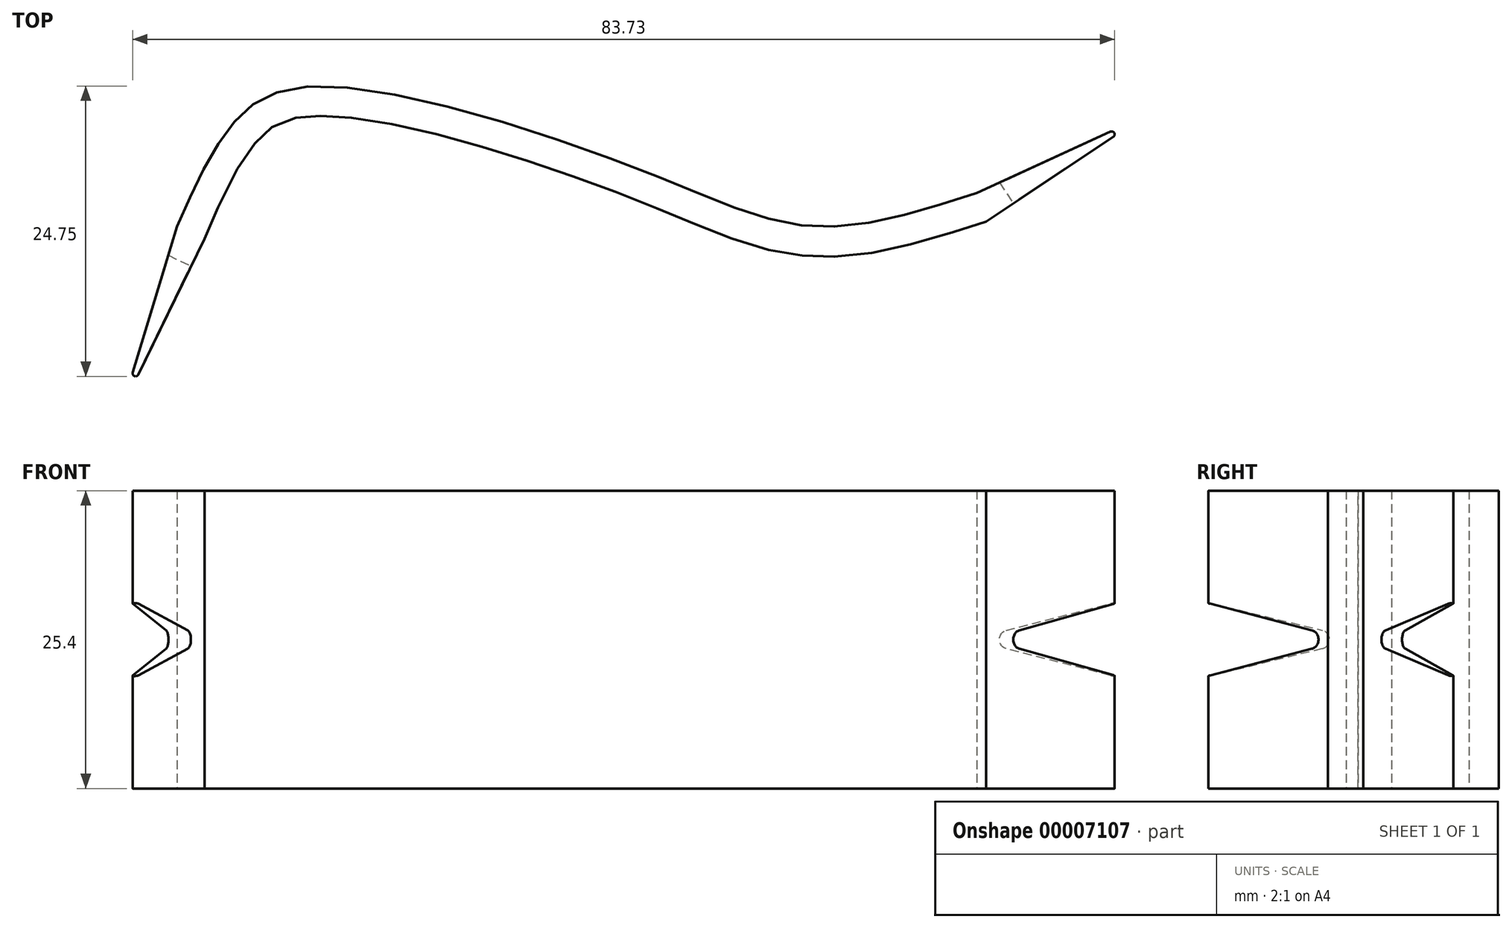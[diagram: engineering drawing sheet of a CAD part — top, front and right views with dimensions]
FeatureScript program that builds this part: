
annotation { "Feature Type Name" : "Feature", "Feature Type Description" : "" }
export const myFeature = defineFeature(function(context is Context, id is Id, definition is map)
    precondition{}
    {
        {
            var Q0;
            Q0=qCreatedBy(makeId("Top.planeOp"),FACE);
            var sketch = newSketch(context, id + "F0", { "sketchPlane" : qUnion([Q0])});
            skFitSpline(sketch, "E0", {"points": [v(0, 0) * mm, v(4.54, 8.52) * mm, v(11.67, 11.97) * mm, v(39.9, 4.7) * mm, v(54.55, 0) * mm, v(68.2, 2.86) * mm], "startDerivative": vector(25.3, 57.5) * mm, "endDerivative": vector(71.65, 23.12) * mm});
            skFitSpline(sketch, "E1.0", {"points": [v(2.33, -1.02) * mm, v(2.85, 0.18) * mm, v(3.89, 2.52) * mm, v(5.22, 5.08) * mm, v(6.2, 6.52) * mm, v(6.75, 7.22) * mm, v(7.3, 7.82) * mm, v(7.98, 8.4) * mm, v(8.9, 8.92) * mm, v(9.87, 9.23) * mm, v(10.88, 9.38) * mm, v(11.76, 9.44) * mm, v(12.78, 9.44) * mm, v(14.32, 9.35) * mm, v(16.52, 9.07) * mm, v(19.5, 8.5) * mm, v(22.68, 7.73) * mm, v(26, 6.81) * mm, v(29.34, 5.78) * mm, v(32.65, 4.68) * mm, v(35.82, 3.54) * mm, v(38.77, 2.42) * mm, v(41.42, 1.35) * mm, v(43.86, 0.34) * mm, v(46.14, -0.58) * mm, v(48.35, -1.38) * mm, v(50.55, -2.01) * mm, v(52.42, -2.37) * mm, v(53.96, -2.52) * mm, v(55.53, -2.58) * mm, v(57.48, -2.47) * mm, v(59.82, -2.13) * mm, v(62.13, -1.61) * mm, v(65.2, -0.78) * mm, v(67.48, -0.04) * mm, v(68.97, 0.44) * mm]});
            skLineSegment(sketch, "E2", {"start": v(68.2, 2.86) * mm, "end": v(82.55, 9.46) * mm});
            skLineSegment(sketch, "E3", {"start": v(82.55, 9.46) * mm, "end": v(68.97, 0.44) * mm});
            skLineSegment(sketch, "E4", {"start": v(0, 0) * mm, "end": v(-4.72, -15.53) * mm});
            skLineSegment(sketch, "E5", {"start": v(-4.72, -15.53) * mm, "end": v(2.33, -1.02) * mm});
            skSolve(sketch);
        }
        {
            var Q0;
            Q0 = qSketchRegion(id + "F0", true);
            extrude(context, id + "F1", {"entities" : qUnion([Q0]), "depth" : 25.4 * mm});
        }
        {
            var Q0;
            Q0=makeQuery(id+"F1.opExtrude","SWEPT_FACE",FACE,{"disambiguationData":[OSD([sQuery(id+"F0.wireOp",EDGE,"E5")])]});
            var sketch = newSketch(context, id + "F2", { "sketchPlane" : qUnion([Q0])});
            skLineSegment(sketch, "E6", {"start": v(-16.03, 16.51) * mm, "end": v(-3.15, 13.49) * mm});
            skLineSegment(sketch, "E7", {"start": v(-3.15, 11.91) * mm, "end": v(-16.03, 8.89) * mm});
            skLineSegment(sketch, "E8", {"start": v(-16.03, 8.9) * mm, "end": v(-16.03, 16.51) * mm});
            skLineSegment(sketch, "E9", {"start": v(-16.03, 16.51) * mm, "end": v(-16.03, 25.4) * mm, "construction": true});
            skLineSegment(sketch, "E10", {"start": v(-16.03, 25.4) * mm, "end": v(-16.03, 16.51) * mm, "construction": true});
            skLineSegment(sketch, "E11", {"start": v(-16.03, 8.9) * mm, "end": v(-16.03, 0) * mm, "construction": true});
            skPoint(sketch, "E12.visualSharp", {"position": v(0.2, 12.7) * mm});
            skArc(sketch, "E12.filletArc", {"start": v(-3.15, 11.91) * mm, "mid": v(-2.53, 12.7) * mm, "end": v(-3.15, 13.49) * mm});
            skLineSegment(sketch, "E13", {"start": v(-16.03, 12.7) * mm, "end": v(-3.33, 12.7) * mm, "construction": true});
            skSolve(sketch);
        }
        {
            var Q0;
            Q0 = qSketchRegion(id + "F2", true);
            extrude(context, id + "F3", {"entities" : qUnion([Q0]), "operationType" : NewBodyOperationType.REMOVE, "oppositeDirection" : true, "depth" : 25.4 * mm});
        }
        {
            var Q0;
            Q0=makeQuery(id+"F1.opExtrude","SWEPT_FACE",FACE,{"disambiguationData":[OSD([sQuery(id+"F0.wireOp",EDGE,"E3")])]});
            var sketch = newSketch(context, id + "F4", { "sketchPlane" : qUnion([Q0])});
            skLineSegment(sketch, "E14", {"start": v(73.99, 16.51) * mm, "end": v(61.1, 13.49) * mm});
            skLineSegment(sketch, "E15", {"start": v(61.1, 11.91) * mm, "end": v(73.99, 8.89) * mm});
            skLineSegment(sketch, "E16", {"start": v(73.99, 8.9) * mm, "end": v(73.99, 16.51) * mm});
            skPoint(sketch, "E17.visualSharp", {"position": v(57.75, 12.7) * mm});
            skArc(sketch, "E17.filletArc", {"start": v(61.1, 13.49) * mm, "mid": v(60.48, 12.7) * mm, "end": v(61.1, 11.91) * mm});
            skLineSegment(sketch, "E18", {"start": v(73.99, 16.51) * mm, "end": v(73.99, 25.4) * mm, "construction": true});
            skLineSegment(sketch, "E19", {"start": v(73.99, 8.9) * mm, "end": v(73.99, 0) * mm, "construction": true});
            skLineSegment(sketch, "E20", {"start": v(61.29, 12.7) * mm, "end": v(73.99, 12.7) * mm, "construction": true});
            skSolve(sketch);
        }
        {
            var Q0;
            Q0 = qSketchRegion(id + "F4", true);
            extrude(context, id + "F5", {"entities" : qUnion([Q0]), "operationType" : NewBodyOperationType.REMOVE, "oppositeDirection" : true, "depth" : 25.4 * mm});
        }
        {
            var Q0;
            {var subQ0=sQuery(id+"F0.wireOp",EDGE,"E4");var subQ1=sQuery(id+"F0.wireOp",EDGE,"E5");Q0=makeQuery(id+"F3.boolean.opBoolean","SPLIT",EDGE,{"disambiguationData":[TD([makeQuery(id+"F3.opExtrude","SWEPT_FACE",FACE,{"disambiguationData":[OSD([sQuery(id+"F2.wireOp",EDGE,"E6")])]})])],"derivedFrom":makeQuery(id+"F1.opExtrude","SWEPT_EDGE",EDGE,{"disambiguationData":[OSD([subQ0,subQ1])]})});}
            var Q1;
            {var subQ0=sQuery(id+"F0.wireOp",EDGE,"E4");var subQ1=sQuery(id+"F0.wireOp",EDGE,"E5");Q1=makeQuery(id+"F3.boolean.opBoolean","SPLIT",EDGE,{"disambiguationData":[TD([makeQuery(id+"F3.opExtrude","SWEPT_FACE",FACE,{"disambiguationData":[OSD([sQuery(id+"F2.wireOp",EDGE,"E7")])]})])],"derivedFrom":makeQuery(id+"F1.opExtrude","SWEPT_EDGE",EDGE,{"disambiguationData":[OSD([subQ0,subQ1])]})});}
            var Q2;
            {var subQ0=sQuery(id+"F0.wireOp",EDGE,"E2");var subQ1=sQuery(id+"F0.wireOp",EDGE,"E3");Q2=makeQuery(id+"F5.boolean.opBoolean","SPLIT",EDGE,{"disambiguationData":[TD([makeQuery(id+"F5.opExtrude","SWEPT_FACE",FACE,{"disambiguationData":[OSD([sQuery(id+"F4.wireOp",EDGE,"E14")])]})])],"derivedFrom":makeQuery(id+"F1.opExtrude","SWEPT_EDGE",EDGE,{"disambiguationData":[OSD([subQ0,subQ1])]})});}
            var Q3;
            {var subQ0=sQuery(id+"F0.wireOp",EDGE,"E2");var subQ1=sQuery(id+"F0.wireOp",EDGE,"E3");Q3=makeQuery(id+"F5.boolean.opBoolean","SPLIT",EDGE,{"disambiguationData":[TD([makeQuery(id+"F5.opExtrude","SWEPT_FACE",FACE,{"disambiguationData":[OSD([sQuery(id+"F4.wireOp",EDGE,"E15")])]})])],"derivedFrom":makeQuery(id+"F1.opExtrude","SWEPT_EDGE",EDGE,{"disambiguationData":[OSD([subQ0,subQ1])]})});}
            fillet(context, id + "F6", {"entities" : qUnion([Q0, Q1, Q2, Q3]), "radius" : 0.25 * mm, "tangentPropagation" : true, "allowEdgeOverflow" : false});
        }
    });
